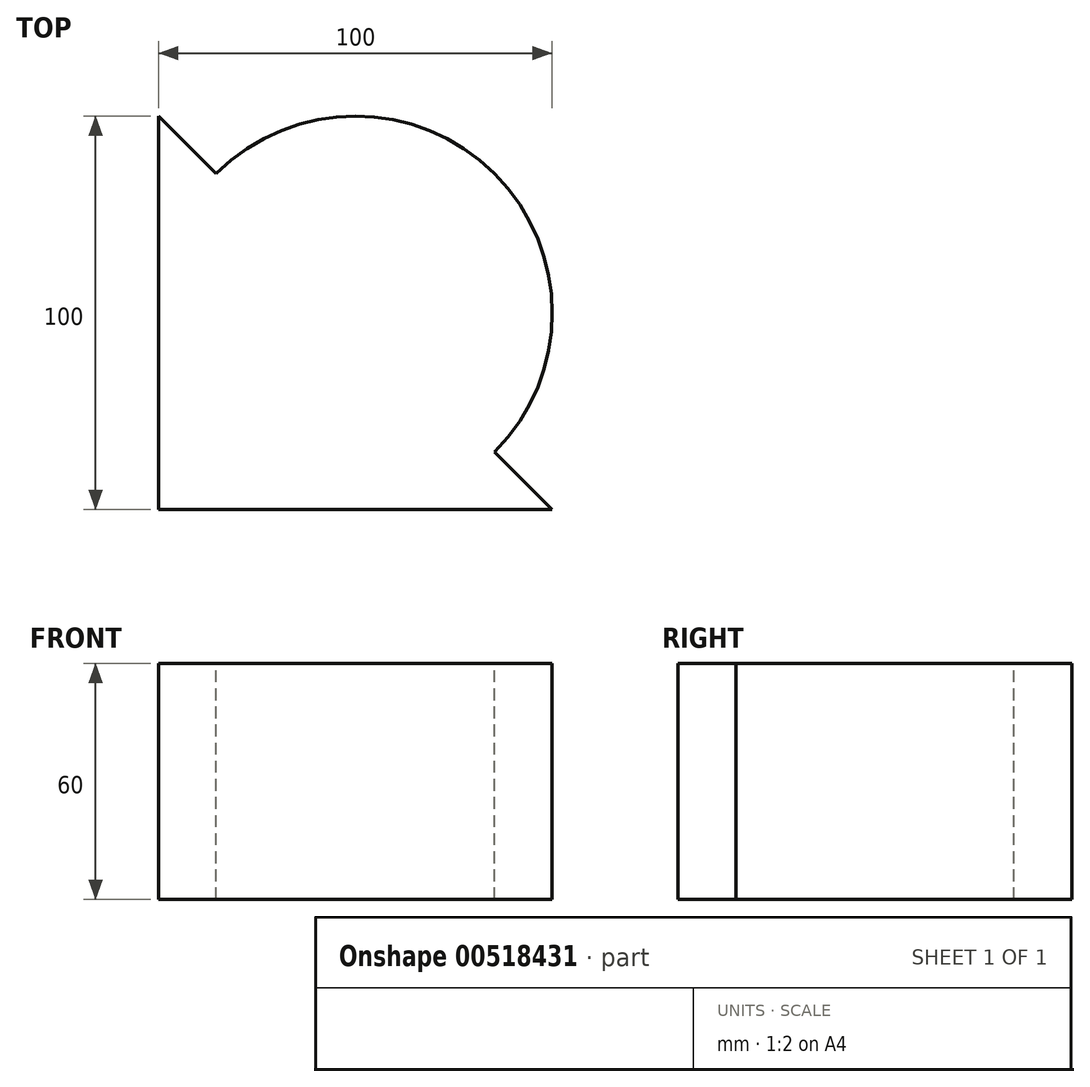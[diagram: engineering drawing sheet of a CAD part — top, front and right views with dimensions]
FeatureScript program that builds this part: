
annotation { "Feature Type Name" : "Feature", "Feature Type Description" : "" }
export const myFeature = defineFeature(function(context is Context, id is Id, definition is map)
    precondition{}
    {
        {
            var Q0;
            Q0=qCreatedBy(makeId("Top.planeOp"),FACE);
            var sketch = newSketch(context, id + "F0", { "sketchPlane" : qUnion([Q0])});
            skLineSegment(sketch, "E0.bottom", {"start": v(0, 0) * mm, "end": v(100, 0) * mm});
            skLineSegment(sketch, "E0.top", {"start": v(0, 100) * mm, "end": v(100, 100) * mm});
            skLineSegment(sketch, "E0.left", {"start": v(0, 0) * mm, "end": v(0, 100) * mm});
            skLineSegment(sketch, "E0.right", {"start": v(100, 0) * mm, "end": v(100, 100) * mm});
            skSolve(sketch);
        }
        {
            var Q0;
            Q0 = qSketchRegion(id + "F0", true);
            extrude(context, id + "F1", {"entities" : qUnion([Q0]), "depth" : 60 * mm, "offsetDistance" : 25 * mm});
        }
        {
            var Q0;
            Q0=makeQuery(id+"F1.opExtrude","CAP_FACE",FACE,{"disambiguationData":[OSD([sQuery(id+"F0.wireOp",EDGE,"E0.bottom"),sQuery(id+"F0.wireOp",EDGE,"E0.top"),sQuery(id+"F0.wireOp",EDGE,"E0.left"),sQuery(id+"F0.wireOp",EDGE,"E0.right")])],"isStart":false});
            var sketch = newSketch(context, id + "F2", { "sketchPlane" : qUnion([Q0])});
            skLineSegment(sketch, "E1", {"start": v(0, 100) * mm, "end": v(100, 0) * mm});
            skSolve(sketch);
        }
        {
            var Q0;
            Q0=makeQuery(id+"F2.imprint","IMPRINT",FACE,{"disambiguationData":[TD([[makeQuery(id+"F2.imprint","IMPRINT",EDGE,{"derivedFrom":sQuery(id+"F2.wireOp",EDGE,"E1")}),1.0]])]});
            var sketch = newSketch(context, id + "F3", { "sketchPlane" : qUnion([Q0])});
            skCircle(sketch, "E2", {"center": v(50, 50) * mm, "radius": 50 * mm});
            skSolve(sketch);
        }
        {
            var Q0;
            {var subQ0=sQuery(id+"F3.wireOp",EDGE,"E2");var subQ1=makeQuery(id+"F2.imprint","IMPRINT",EDGE,{"derivedFrom":makeQuery(id+"F1.opExtrude","CAP_EDGE",EDGE,{"disambiguationData":[OSD([sQuery(id+"F0.wireOp",EDGE,"E0.top")])],"isStart":false})});var subQ2=makeQuery(id+"F3.imprint","INTERSECT",VERTEX,{"derivedFrom":[subQ1,subQ0]});Q0=makeQuery(id+"F3.imprint","IMPRINT",FACE,{"disambiguationData":[TD([[makeQuery(id+"F3.imprint","IMPRINT",EDGE,{"disambiguationData":[TD([[subQ2,1.0]])],"derivedFrom":subQ0}),-1.0]])]});}
            var Q1;
            {var subQ0=sQuery(id+"F3.wireOp",EDGE,"E2");var subQ1=makeQuery(id+"F2.imprint","IMPRINT",EDGE,{"derivedFrom":makeQuery(id+"F1.opExtrude","CAP_EDGE",EDGE,{"disambiguationData":[OSD([sQuery(id+"F0.wireOp",EDGE,"E0.right")])],"isStart":false})});var subQ2=makeQuery(id+"F3.imprint","INTERSECT",VERTEX,{"derivedFrom":[subQ1,subQ0]});Q1=makeQuery(id+"F3.imprint","IMPRINT",FACE,{"disambiguationData":[TD([[makeQuery(id+"F3.imprint","IMPRINT",EDGE,{"disambiguationData":[TD([[subQ2,1.0]])],"derivedFrom":subQ0}),-1.0]])]});}
            var Q2;
            {var subQ0=sQuery(id+"F3.wireOp",EDGE,"E2");var subQ1=makeQuery(id+"F2.imprint","IMPRINT",EDGE,{"derivedFrom":makeQuery(id+"F1.opExtrude","CAP_EDGE",EDGE,{"disambiguationData":[OSD([sQuery(id+"F0.wireOp",EDGE,"E0.top")])],"isStart":false})});var subQ2=makeQuery(id+"F3.imprint","INTERSECT",VERTEX,{"derivedFrom":[subQ1,subQ0]});Q2=makeQuery(id+"F3.imprint","IMPRINT",FACE,{"disambiguationData":[TD([[makeQuery(id+"F3.imprint","IMPRINT",EDGE,{"disambiguationData":[TD([[subQ2,-1.0]])],"derivedFrom":subQ0}),-1.0]])]});}
            extrude(context, id + "F4", {"entities" : qUnion([Q0, Q1, Q2]), "operationType" : NewBodyOperationType.REMOVE, "endBound" : BoundingType.THROUGH_ALL, "oppositeDirection" : true, "depth" : 25 * mm, "offsetDistance" : 25 * mm});
        }
    });
